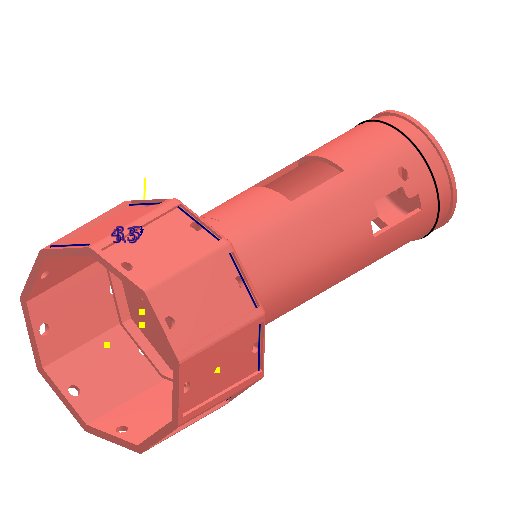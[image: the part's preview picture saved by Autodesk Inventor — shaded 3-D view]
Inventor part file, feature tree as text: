
AUTODESK INVENTOR PART (.ipt)
format: ipt  version: 2025 (Build 290162000, 162)  size: 1,868,800 bytes
history: native  units: in
note: dims shown in document units (in); Inventor stores cm internally (conversion verified against a paired STEP export)
features: sketch x60, extrude x56, fillet x9, plane x6, other x3, direct_edit x2, pattern_circular x2, move_body x2, reference x2, emboss x1, split x1, projected_geometry x1
ambient origin geometry x8: Origin, YZ Plane, XZ Plane, XY Plane, X Axis, Y Axis, Z Axis, Center Point
bodies: Solid1 (feature_tree), Body4 (feature_tree), Solid2 (feature_tree), Solid3 (feature_tree)
feature tree (145):
  direct_edit  "Direct Edit1"
  extrude  "Extrusion1"  Depth=0.2062in TaperAngle=0.0deg
  extrude  "Extrusion2"  Depth=0.1437in TaperAngle=0.0deg
  sketch  "Sketch3"  dims[d8=0.0787in d9=1.811in d10=0.0in]
  extrude  "Extrusion3"  Depth=1.811in TaperAngle=0.0deg
  sketch  "Sketch6"  dims[d13=0.0591in d14=0.0in d15=0.1969in]
  extrude  "Extrusion4"  Depth=0.9449in
  extrude  "Extrusion5"  Depth=0.1969in
  pattern_circular  "Circular Pattern1"  Count=9  [1 undecoded]
  extrude  "Extrusion6"  Depth=0.315in
  extrude  "Extrusion7"  Depth=1.4409in TaperAngle=0.0deg
  pattern_circular  "Circular Pattern2"  Count=9  [1 undecoded]
  fillet  "Fillet1"  Radius=0.1412in
  extrude  "Extrusion8"  Depth=0.063in
  extrude  "Extrusion9"  Depth=0.8312in TaperAngle=0.0deg
  extrude  "Extrusion10"  Depth=0.0787in
  extrude  "Extrusion11"  Depth=0.1688in TaperAngle=0.0deg
  direct_edit  "Direct Edit2"
  extrude  "Extrusion12"  Depth=1.1063in TaperAngle=0.0deg
  extrude  "Extrusion13"  Depth=0.4724in TaperAngle=0.0deg
  extrude  "Extrusion14"  Depth=1.8898in
  extrude  "Extrusion15"  Depth=1.2795in
  extrude  "Extrusion16"  Depth=0.0787in TaperAngle=0.0deg
  extrude  "Extrusion17"  Depth=0.0787in
  fillet  "Fillet2"  Radius=0.0787in
  fillet  "Fillet3"  Radius=0.0787in
  fillet  "Fillet4"  Radius=0.7338in
  fillet  "Fillet5"  Radius=0.3937in
  extrude  "Extrusion18"  Depth=0.8312in TaperAngle=0.0deg
  extrude  "Extrusion19"  Depth=0.1575in TaperAngle=0.0deg
  extrude  "Extrusion20"  Depth=0.1969in TaperAngle=0.0deg
  fillet  "Fillet6"  Radius=0.1781in
  sketch  "Sketch24"  dims[d78=1.3912in d79=0.1969in d80=0.0in d81=0.1781in d82=0.0in]
  extrude  "Extrusion22"  Depth=1.5438in TaperAngle=0.0deg
  fillet  "Fillet8"  Radius=2.7938in
  extrude  "Extrusion23"  Depth=0.2362in
  extrude  "Extrusion24"  Depth=1.7313in TaperAngle=0.0deg
  extrude  "Extrusion25"  Depth=0.1575in
  sketch  "Sketch30"  dims[d98=0.1575in d99=1.6334in d100=0.0in]
  sketch  "Sketch32"  dims[d101=3.5084in d102=0.0in d103=0.9459in d104=0.6917in d105=0.0in d106=0.0in]
  extrude  "Extrusion26"  Depth=1.6334in TaperAngle=0.0deg
  extrude  "Extrusion27"  Depth=0.9459in TaperAngle=0.0deg
  plane  "Work Plane3"
  extrude  "Extrusion28"  Depth=0.0787in TaperAngle=0.0deg
  sketch  "Sketch37"  dims[d118=0.0in d119=0.0in d120=0.0in d121=-0.3937in]
  extrude  "Extrusion29"  Depth=0.9375in
  extrude  "Extrusion30"  Depth=1.3563in TaperAngle=0.0deg
  extrude  "Extrusion31"  TaperAngle=0.0deg  [1 undecoded]
  extrude  "Extrusion32"  Depth=1.4562in TaperAngle=0.0deg
  sketch  "Sketch42"  dims[d136=4.9173in d137=0.0in d138=2.6535in d139=0.0in]
  extrude  "Extrusion33"  Depth=4.4562in TaperAngle=0.0deg
  sketch  "Sketch44"  dims[d144=0.6063in d145=0.0in d146=0.1378in]
  sketch  "Sketch45"  dims[d147=3.4188in d148=0.0in d149=0.2687in d150=0.0in]
  extrude  "Extrusion34"  Depth=0.9173in TaperAngle=0.0deg
  extrude  "Extrusion35"  Depth=2.6535in TaperAngle=0.0deg
  plane  "Work Plane6"
  plane  "Work Plane7"
  extrude  "Extrusion36"  Depth=4.4562in TaperAngle=0.0deg
  sketch  "Sketch49"  dims[d163=0.2062in d164=0.0in d165=0.2062in d166=0.0in]
  plane  "Work Plane8"
  emboss  "Emboss1"
  extrude  "Extrusion37"  Depth=0.1378in
  plane  "Work Plane9"
  split  "Split1"
  move_body  "Move Body1"
  extrude  "Extrusion38"  Depth=0.2687in TaperAngle=0.0deg
  extrude  "Extrusion39"  Depth=3.5438in TaperAngle=0.0deg
  sketch  "Sketch54"
  extrude  "Extrusion40"  Depth=0.0812in TaperAngle=0.0deg
  extrude  "Extrusion41"  Depth=0.2953in TaperAngle=0.0deg
  extrude  "Extrusion42"  Depth=0.2062in TaperAngle=0.0deg
  extrude  "Extrusion43"  Depth=0.0787in
  extrude  "Extrusion44"  [1 undecoded]
  extrude  "Extrusion45"  [1 undecoded]
  extrude  "Extrusion46"  [1 undecoded]
  extrude  "Extrusion47"  [1 undecoded]
  sketch  "Sketch56"
  extrude  "Extrusion48"  [1 undecoded]
  extrude  "Extrusion49"  [1 undecoded]
  extrude  "Extrusion50"  [1 undecoded]
  extrude  "Extrusion51"  [1 undecoded]
  extrude  "Extrusion52"  [1 undecoded]
  extrude  "Extrusion53"  [1 undecoded]
  extrude  "Extrusion54"  [1 undecoded]
  extrude  "Extrusion55"  [1 undecoded]
  extrude  "Extrusion56"  [1 undecoded]
  fillet  "Fillet13"  [1 undecoded]
  fillet  "Fillet14"  [1 undecoded]
  extrude  "Extrusion57"  [1 undecoded]
  sketch  "Sketch1"  dims[d0=0.0in d1=0.0in d2=-0.6875in d3=0.2062in d4=0.0in]
  sketch  "Sketch2"  dims[d5=1.1811in d6=0.1437in d7=0.0in]
  sketch  "Sketch5"  dims[d11=1.7323in d12=0.9449in]
  sketch  "Sketch7"  dims[d16=0.1969in]
  sketch  "Sketch8"  dims[d17=0.1841in d18=0.0in d19=3.5433in d20=2.4737in]
  sketch  "Sketch9"  dims[d22=0.0787in d23=0.315in]
  sketch  "Sketch10"  dims[d24=0.0787in d25=1.4409in d26=0.0in]
  sketch  "Sketch11"  dims[d27=1.9966in d28=0.0in d29=3.5433in d30=2.4737in d32=0.1412in]
  sketch  "Sketch12"  dims[d33=0.063in d34=0.063in]
  sketch  "Sketch13"  dims[d35=0.2756in d36=0.0in d37=0.8312in d38=0.0in]
  sketch  "Sketch14"  dims[d39=1.1063in d40=0.0in d41=0.0787in]
  sketch  "Sketch15"  dims[d42=0.0787in d43=0.1688in d44=0.0in]
  sketch  "Sketch16"  dims[d45=0.5187in d46=0.0in d47=1.1063in d48=0.0in]
  sketch  "Sketch17"  dims[d49=1.6535in d50=0.4724in d51=0.0in]
  sketch  "Sketch18"  dims[d52=0.0787in d53=0.0in d54=1.8898in]
  sketch  "Sketch19"  dims[d55=0.2963in d56=0.0in d57=1.2795in]
  sketch  "Sketch20"  dims[d58=1.3583in d59=0.0787in d60=0.0in]
  sketch  "Sketch21"  dims[d61=0.0787in d62=0.0787in d63=0.0787in d64=0.0787in d65=0.7338in d66=0.0in d67=0.3937in d68=0.0in]
  sketch  "Sketch22"  dims[d69=0.0787in d70=0.8312in d71=0.0in]
  sketch  "Sketch23"  dims[d72=0.0787in d76=0.1575in d77=0.0in]
  sketch  "Sketch26"  dims[d83=0.1575in d84=0.0in d85=1.5438in d86=0.0in d87=2.7938in d88=0.0in]
  sketch  "Sketch27"  dims[d89=1.7313in d90=0.0in d91=0.2362in]
  sketch  "Sketch28"  dims[d92=0.2362in d93=1.7313in d94=0.0in]
  sketch  "Sketch29"  dims[d95=0.0709in d96=0.0in d97=0.1575in]
  sketch  "Sketch33"  dims[d107=0.1137in d108=0.0in d109=0.0787in d110=0.0in]
  sketch  "Sketch34"  dims[d111=1.6688in d112=0.0in d113=0.9375in]
  sketch  "Sketch36"  dims[d114=0.0394in d115=0.0in d116=1.3563in d117=0.0in]
  reference  "Reference1"
  reference  "Reference2"
  sketch  "Sketch39"  dims[d122=0.3937in d123=0.0in d124=1.4562in d125=0.0in]
  sketch  "Sketch40"  dims[d130=0.1693in d131=4.4562in d132=0.0in]
  sketch  "Sketch41"  dims[d133=0.2165in d134=0.9173in d135=0.0in]
  sketch  "Sketch43"  dims[d140=0.9247in d141=0.0in d142=4.4562in d143=0.0in]
  sketch  "Sketch46"  dims[d151=0.4813in d152=0.0in d153=3.5438in d154=0.0in]
  sketch  "Sketch47"  dims[d155=0.3937in d156=0.0in d157=0.0812in d158=0.0in]
  plane  "Work Plane5"
  sketch  "Sketch48"  dims[d159=0.2953in d160=0.0in d161=0.2953in d162=0.0in]
  sketch  "Sketch50"  dims[d167=0.0787in d168=0.0787in]
  sketch  "Sketch51"  dims[d169=1.7313in d170=0.0in]
  sketch  "Sketch52"
  sketch  "Sketch53"
  sketch  "Sketch55"
  sketch  "Sketch57"
  sketch  "Sketch58"
  sketch  "Sketch59"
  sketch  "Sketch60"
  sketch  "Sketch61"
  sketch  "Sketch62"
  sketch  "Sketch63"
  sketch  "Sketch64"
  sketch  "Sketch65"
  move_body  "Move1"
  projected_geometry  "Project Cut Edges1"
  other  "Delete1"
  other  "Full assembly 2.iam"
  other  "main_board:1"
note: 19 required parameter values undecoded (feature->parameter linkage not recoverable at this tier; creation-order binding heuristic only, values carry confidence <= 0.55)
